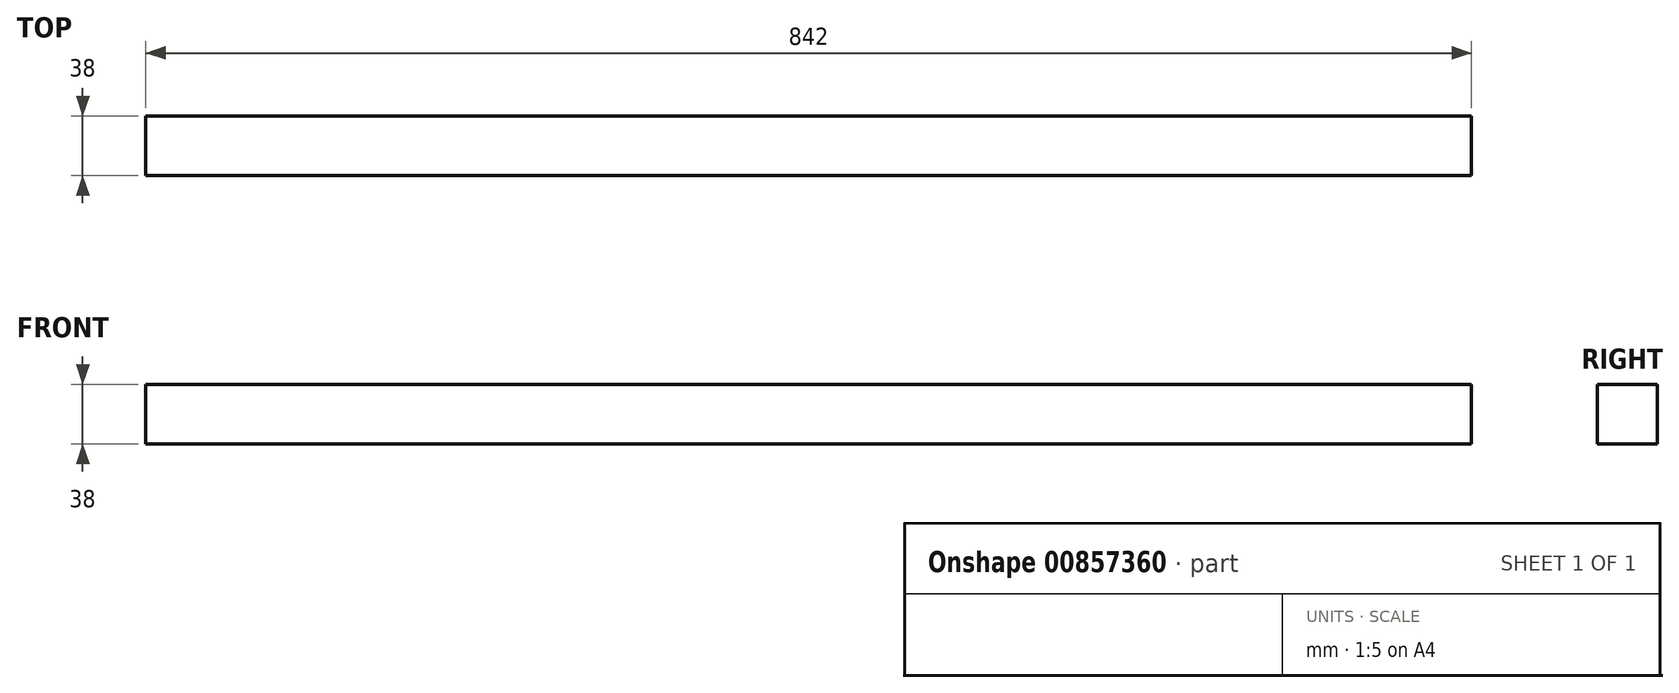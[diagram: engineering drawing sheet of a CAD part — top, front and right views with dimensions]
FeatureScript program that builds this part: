
annotation { "Feature Type Name" : "Feature", "Feature Type Description" : "" }
export const myFeature = defineFeature(function(context is Context, id is Id, definition is map)
    precondition{}
    {
        {
            var Q0;
            Q0=qCreatedBy(makeId("Right.planeOp"),FACE);
            var sketch = newSketch(context, id + "F0", { "sketchPlane" : qUnion([Q0])});
            skLineSegment(sketch, "E0.bottom", {"start": v(-19, 19) * mm, "end": v(19, 19) * mm});
            skLineSegment(sketch, "E0.top", {"start": v(-19, -19) * mm, "end": v(19, -19) * mm});
            skLineSegment(sketch, "E0.left", {"start": v(-19, 19) * mm, "end": v(-19, -19) * mm});
            skLineSegment(sketch, "E0.right", {"start": v(19, 19) * mm, "end": v(19, -19) * mm});
            skSolve(sketch);
        }
        {
            var Q0;
            Q0=makeQuery(id+"F0.imprint","IMPRINT",FACE,{"disambiguationData":[TD([[makeQuery(id+"F0.imprint","IMPRINT",EDGE,{"derivedFrom":sQuery(id+"F0.wireOp",EDGE,"E0.bottom")}),-1.0]])]});
            extrude(context, id + "F1", {"entities" : qUnion([Q0]), "depth" : 842 * mm, "offsetDistance" : 25 * mm});
        }
    });
